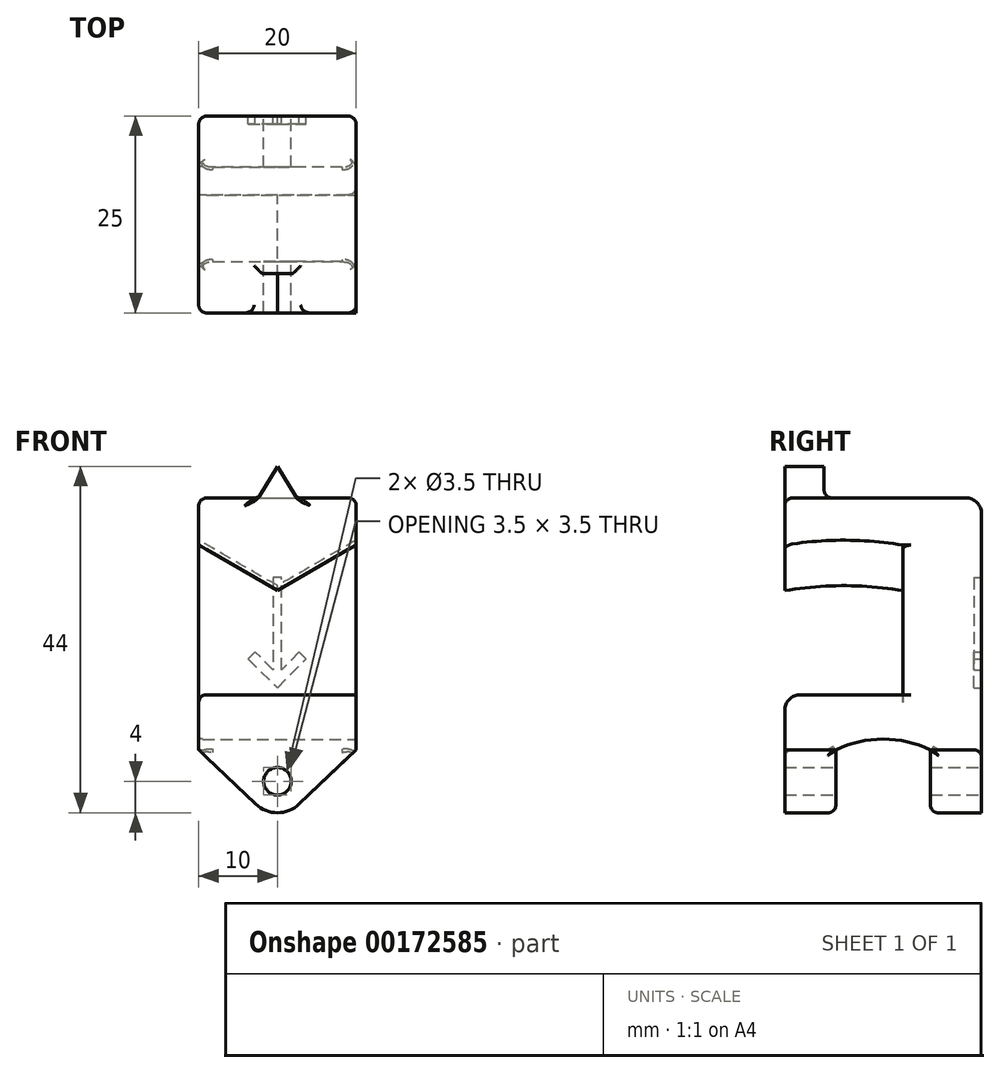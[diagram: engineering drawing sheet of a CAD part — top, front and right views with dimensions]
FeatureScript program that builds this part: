
annotation { "Feature Type Name" : "Feature", "Feature Type Description" : "" }
export const myFeature = defineFeature(function(context is Context, id is Id, definition is map)
    precondition{}
    {
        {
            var Q0;
            Q0=qCreatedBy(makeId("Front.planeOp"),FACE);
            var sketch = newSketch(context, id + "F0", { "sketchPlane" : qUnion([Q0])});
            skLineSegment(sketch, "E0.bottom", {"start": v(0, 0) * mm, "end": v(20, 0) * mm});
            skLineSegment(sketch, "E0.top", {"start": v(0, 40) * mm, "end": v(20, 40) * mm});
            skLineSegment(sketch, "E0.left", {"start": v(0, 0) * mm, "end": v(0, 40) * mm});
            skLineSegment(sketch, "E0.right", {"start": v(20, 0) * mm, "end": v(20, 40) * mm});
            skSolve(sketch);
        }
        {
            var Q0;
            Q0=qSketchRegion(id+"F0",true);
            extrude(context, id + "F1", {"entities" : qUnion([Q0]), "depth" : 10 * mm});
        }
        {
            var Q0;
            Q0=makeQuery(id+"F1.opExtrude","CAP_FACE",FACE,{"disambiguationData":[OSD([sQuery(id+"F0.wireOp",EDGE,"E0.bottom"),sQuery(id+"F0.wireOp",EDGE,"E0.top"),sQuery(id+"F0.wireOp",EDGE,"E0.left"),sQuery(id+"F0.wireOp",EDGE,"E0.right")])],"isStart":false});
            var sketch = newSketch(context, id + "F2", { "sketchPlane" : qUnion([Q0])});
            skLineSegment(sketch, "E1", {"start": v(0, 40) * mm, "end": v(20, 40) * mm});
            skLineSegment(sketch, "E2", {"start": v(20, 40) * mm, "end": v(20, 34) * mm});
            skLineSegment(sketch, "E3", {"start": v(20, 34) * mm, "end": v(10, 28.23) * mm});
            skPoint(sketch, "E3.endSnap0", {"position": v(10, 40) * mm});
            skLineSegment(sketch, "E4", {"start": v(10, 28.23) * mm, "end": v(0, 34) * mm});
            skLineSegment(sketch, "E5", {"start": v(0, 34) * mm, "end": v(0, 40) * mm});
            skLineSegment(sketch, "E6.bottom", {"start": v(0, 0) * mm, "end": v(20, 0) * mm});
            skLineSegment(sketch, "E6.top", {"start": v(0, 15) * mm, "end": v(20, 15) * mm});
            skLineSegment(sketch, "E6.left", {"start": v(0, 0) * mm, "end": v(0, 15) * mm});
            skLineSegment(sketch, "E6.right", {"start": v(20, 0) * mm, "end": v(20, 15) * mm});
            skSolve(sketch);
        }
        {
            var Q0;
            Q0=qSketchRegion(id+"F2",true);
            extrude(context, id + "F3", {"entities" : qUnion([Q0]), "operationType" : NewBodyOperationType.ADD, "depth" : 15 * mm});
        }
        {
            var Q0;
            Q0=makeQuery(id+"F3.boolean.opBoolean","MERGE",FACE,{"derivedFrom":[makeQuery(id+"F1.opExtrude","SWEPT_FACE",FACE,{"disambiguationData":[OSD([sQuery(id+"F0.wireOp",EDGE,"E0.right")])]}),makeQuery(id+"F3.opExtrude","SWEPT_FACE",FACE,{"disambiguationData":[OSD([sQuery(id+"F2.wireOp",EDGE,"E2")])]}),makeQuery(id+"F3.opExtrude","SWEPT_FACE",FACE,{"disambiguationData":[OSD([sQuery(id+"F2.wireOp",EDGE,"E6.right")])]})]});
            var sketch = newSketch(context, id + "F4", { "sketchPlane" : qUnion([Q0])});
            skLineSegment(sketch, "E7.bottom", {"start": v(-18.5, 0) * mm, "end": v(-6.5, 0) * mm});
            skLineSegment(sketch, "E7.top", {"start": v(-18.5, 8) * mm, "end": v(-6.5, 8) * mm});
            skLineSegment(sketch, "E7.left", {"start": v(-18.5, 0) * mm, "end": v(-18.5, 8) * mm});
            skLineSegment(sketch, "E7.right", {"start": v(-6.5, 0) * mm, "end": v(-6.5, 8) * mm});
            skArc(sketch, "E8", {"start": v(-6.5, 8) * mm, "mid": v(-12.5, 9.35) * mm, "end": v(-18.5, 8) * mm});
            skSolve(sketch);
        }
        {
            var Q0;
            Q0=qSketchRegion(id+"F4",true);
            extrude(context, id + "F5", {"entities" : qUnion([Q0]), "operationType" : NewBodyOperationType.REMOVE, "oppositeDirection" : true, "depth" : 25 * mm});
        }
        {
            var Q0;
            Q0=makeQuery(id+"F5.boolean.opBoolean","COPY",FACE,{"derivedFrom":makeQuery(id+"F5.opExtrude","SWEPT_FACE",FACE,{"disambiguationData":[OSD([sQuery(id+"F4.wireOp",EDGE,"E7.left")])]})});
            var sketch = newSketch(context, id + "F6", { "sketchPlane" : qUnion([Q0])});
            skCircle(sketch, "E9", {"center": v(-10, 4) * mm, "radius": 1.75 * mm});
            skPoint(sketch, "E9.centerSnap0", {"position": v(-20, 4) * mm});
            skPoint(sketch, "E9.centerSnap1", {"position": v(-10, 0) * mm});
            skSolve(sketch);
        }
        {
            var Q0;
            Q0=qSketchRegion(id+"F6",true);
            extrude(context, id + "F7", {"entities" : qUnion([Q0]), "operationType" : NewBodyOperationType.REMOVE, "oppositeDirection" : true, "depth" : 25 * mm, "hasSecondDirection" : true, "secondDirectionOppositeDirection" : false, "secondDirectionDepth" : 25 * mm});
        }
        {
            var Q0;
            Q0=makeQuery(id+"F3.opExtrude","CAP_FACE",FACE,{"disambiguationData":[OSD([sQuery(id+"F2.wireOp",EDGE,"E6.bottom"),sQuery(id+"F2.wireOp",EDGE,"E6.top"),sQuery(id+"F2.wireOp",EDGE,"E6.left"),sQuery(id+"F2.wireOp",EDGE,"E6.right")])],"isStart":false});
            var sketch = newSketch(context, id + "F8", { "sketchPlane" : qUnion([Q0])});
            skArc(sketch, "E10", {"start": v(10, 0) * mm, "mid": v(11.49, 0.29) * mm, "end": v(12.76, 1.1) * mm});
            skLineSegment(sketch, "E11", {"start": v(12.76, 1.1) * mm, "end": v(20, 8) * mm});
            skLineSegment(sketch, "E12", {"start": v(10, 4) * mm, "end": v(10, 0) * mm, "construction": true});
            skLineSegment(sketch, "E13.MirrorCS", {"start": v(7.24, 1.1) * mm, "end": v(0, 8) * mm});
            skArc(sketch, "E14.MirrorCS", {"start": v(10, 0) * mm, "mid": v(8.51, 0.29) * mm, "end": v(7.24, 1.1) * mm});
            skSolve(sketch);
        }
        {
            var Q0;
            {var subQ0=sQuery(id+"F8.wireOp",EDGE,"E10");Q0=makeQuery(id+"F8.imprint","IMPRINT",FACE,{"disambiguationData":[TD([[makeQuery(id+"F8.imprint","IMPRINT",EDGE,{"derivedFrom":subQ0}),-1.0]])]});}
            var Q1;
            {var subQ0=sQuery(id+"F8.wireOp",EDGE,"E13.MirrorCS");Q1=makeQuery(id+"F8.imprint","IMPRINT",FACE,{"disambiguationData":[TD([[makeQuery(id+"F8.imprint","IMPRINT",EDGE,{"derivedFrom":subQ0}),1.0]])]});}
            extrude(context, id + "F9", {"entities" : qUnion([Q0, Q1]), "operationType" : NewBodyOperationType.REMOVE, "oppositeDirection" : true, "depth" : 25 * mm});
        }
        {
            var Q0;
            Q0=makeQuery(id+"F1.opExtrude","CAP_EDGE",EDGE,{"disambiguationData":[OSD([sQuery(id+"F0.wireOp",EDGE,"E0.top")])],"isStart":true});
            var Q1;
            Q1=makeQuery(id+"F3.opExtrude","CAP_EDGE",EDGE,{"disambiguationData":[OSD([sQuery(id+"F2.wireOp",EDGE,"E6.top")])],"isStart":true});
            var Q2;
            Q2=makeQuery(id+"F3.opExtrude","CAP_EDGE",EDGE,{"disambiguationData":[OSD([sQuery(id+"F2.wireOp",EDGE,"E6.top")])],"isStart":false});
            fillet(context, id + "F10", {"entities" : qUnion([Q0, Q1, Q2]), "radius" : 2 * mm, "tangentPropagation" : true, "allowEdgeOverflow" : false});
        }
        {
            var Q0;
            Q0=makeQuery(id+"F1.opExtrude","CAP_EDGE",EDGE,{"disambiguationData":[OSD([sQuery(id+"F0.wireOp",EDGE,"E0.left")])],"isStart":true});
            var Q1;
            Q1=makeQuery(id+"F1.opExtrude","CAP_EDGE",EDGE,{"disambiguationData":[OSD([sQuery(id+"F0.wireOp",EDGE,"E0.right")])],"isStart":true});
            var Q2;
            Q2=makeQuery(id+"F9.boolean.opBoolean","COPY",EDGE,{"derivedFrom":makeQuery(id+"F9.opExtrude","CAP_EDGE",EDGE,{"disambiguationData":[OSD([sQuery(id+"F8.wireOp",EDGE,"E13.MirrorCS")])],"isStart":false})});
            var Q3;
            Q3=makeQuery(id+"F9.boolean.opBoolean","COPY",EDGE,{"derivedFrom":makeQuery(id+"F9.opExtrude","CAP_EDGE",EDGE,{"disambiguationData":[OSD([sQuery(id+"F8.wireOp",EDGE,"E13.MirrorCS")])],"isStart":true})});
            var Q4;
            Q4=makeQuery(id+"F9.boolean.opBoolean","INTERSECT",EDGE,{"derivedFrom":[makeQuery(id+"F5.boolean.opBoolean","COPY",FACE,{"derivedFrom":makeQuery(id+"F5.opExtrude","SWEPT_FACE",FACE,{"disambiguationData":[OSD([sQuery(id+"F4.wireOp",EDGE,"E7.right")])]})}),makeQuery(id+"F9.opExtrude","SWEPT_FACE",FACE,{"disambiguationData":[OSD([sQuery(id+"F8.wireOp",EDGE,"E13.MirrorCS")])]})]});
            var Q5;
            Q5=makeQuery(id+"F9.boolean.opBoolean","INTERSECT",EDGE,{"derivedFrom":[makeQuery(id+"F5.boolean.opBoolean","COPY",FACE,{"derivedFrom":makeQuery(id+"F5.opExtrude","SWEPT_FACE",FACE,{"disambiguationData":[OSD([sQuery(id+"F4.wireOp",EDGE,"E7.left")])]})}),makeQuery(id+"F9.opExtrude","SWEPT_FACE",FACE,{"disambiguationData":[OSD([sQuery(id+"F8.wireOp",EDGE,"E13.MirrorCS")])]})]});
            var Q6;
            Q6=makeQuery(id+"F3.opExtrude","SWEPT_EDGE",EDGE,{"disambiguationData":[OSD([sQuery(id+"F0.wireOp",EDGE,"E0.left"),sQuery(id+"F2.wireOp",EDGE,"E6.top"),sQuery(id+"F2.wireOp",EDGE,"E6.left")])]});
            var Q7;
            Q7=makeQuery(id+"F1.opExtrude","CAP_EDGE",EDGE,{"disambiguationData":[OSD([sQuery(id+"F0.wireOp",EDGE,"E0.right")])],"isStart":false});
            var Q8;
            Q8=makeQuery(id+"F3.opExtrude","CAP_EDGE",EDGE,{"disambiguationData":[OSD([sQuery(id+"F2.wireOp",EDGE,"E5")])],"isStart":false});
            var Q9;
            Q9=makeQuery(id+"F3.opExtrude","CAP_EDGE",EDGE,{"disambiguationData":[OSD([sQuery(id+"F2.wireOp",EDGE,"E1")])],"isStart":false});
            var Q10;
            Q10=makeQuery(id+"F3.opExtrude","CAP_EDGE",EDGE,{"disambiguationData":[OSD([sQuery(id+"F2.wireOp",EDGE,"E2")])],"isStart":false});
            fillet(context, id + "F11", {"entities" : qUnion([Q0, Q1, Q2, Q3, Q4, Q5, Q6, Q7, Q8, Q9, Q10]), "radius" : 1 * mm, "tangentPropagation" : true, "allowEdgeOverflow" : false});
        }
        {
            var Q0;
            Q0=makeQuery(id+"F5.boolean.opBoolean","COPY",EDGE,{"derivedFrom":makeQuery(id+"F5.opExtrude","SWEPT_EDGE",EDGE,{"disambiguationData":[OSD([sQuery(id+"F4.wireOp",EDGE,"E7.top"),sQuery(id+"F4.wireOp",EDGE,"E7.right")])]})});
            var Q1;
            Q1=makeQuery(id+"F5.boolean.opBoolean","COPY",EDGE,{"derivedFrom":makeQuery(id+"F5.opExtrude","SWEPT_EDGE",EDGE,{"disambiguationData":[OSD([sQuery(id+"F4.wireOp",EDGE,"E7.top"),sQuery(id+"F4.wireOp",EDGE,"E7.left")])]})});
            fillet(context, id + "F12", {"entities" : qUnion([Q0, Q1]), "radius" : 0.5 * mm, "tangentPropagation" : true, "allowEdgeOverflow" : false});
        }
        {
            var Q0;
            Q0=makeQuery(id+"F1.opExtrude","CAP_FACE",FACE,{"disambiguationData":[OSD([sQuery(id+"F0.wireOp",EDGE,"E0.bottom"),sQuery(id+"F0.wireOp",EDGE,"E0.top"),sQuery(id+"F0.wireOp",EDGE,"E0.left"),sQuery(id+"F0.wireOp",EDGE,"E0.right")])],"isStart":true});
            var sketch = newSketch(context, id + "F13", { "sketchPlane" : qUnion([Q0])});
            skLineSegment(sketch, "E15", {"start": v(-9.46, 29.87) * mm, "end": v(-9.46, 18.15) * mm});
            skLineSegment(sketch, "E16", {"start": v(-9.46, 18.15) * mm, "end": v(-7.17, 20.42) * mm});
            skLineSegment(sketch, "E17", {"start": v(-7.17, 20.42) * mm, "end": v(-6.3, 19.54) * mm});
            skLineSegment(sketch, "E18", {"start": v(-6.3, 19.54) * mm, "end": v(-10, 15.87) * mm});
            skLineSegment(sketch, "E19", {"start": v(-10, 15.87) * mm, "end": v(-13.65, 19.54) * mm});
            skLineSegment(sketch, "E20", {"start": v(-13.65, 19.54) * mm, "end": v(-12.76, 20.42) * mm});
            skLineSegment(sketch, "E21", {"start": v(-12.76, 20.42) * mm, "end": v(-10.51, 18.15) * mm});
            skLineSegment(sketch, "E22", {"start": v(-10.51, 18.15) * mm, "end": v(-10.51, 29.87) * mm});
            skLineSegment(sketch, "E23", {"start": v(-10.51, 29.87) * mm, "end": v(-9.46, 29.87) * mm});
            skSolve(sketch);
        }
        {
            var Q0;
            Q0=qSketchRegion(id+"F13",true);
            extrude(context, id + "F14", {"entities" : qUnion([Q0]), "operationType" : NewBodyOperationType.REMOVE, "oppositeDirection" : true, "depth" : 1 * mm});
        }
        {
            var Q0;
            Q0=makeQuery(id+"F3.opExtrude","CAP_FACE",FACE,{"disambiguationData":[OSD([sQuery(id+"F2.wireOp",EDGE,"E1"),sQuery(id+"F2.wireOp",EDGE,"E2"),sQuery(id+"F2.wireOp",EDGE,"E3"),sQuery(id+"F2.wireOp",EDGE,"E4"),sQuery(id+"F2.wireOp",EDGE,"E5")])],"isStart":false});
            var sketch = newSketch(context, id + "F15", { "sketchPlane" : qUnion([Q0])});
            skLineSegment(sketch, "E24", {"start": v(10, 39) * mm, "end": v(13, 39) * mm});
            skLineSegment(sketch, "E25", {"start": v(13, 39) * mm, "end": v(10, 44) * mm});
            skLineSegment(sketch, "E26", {"start": v(10, 44) * mm, "end": v(7, 39) * mm});
            skLineSegment(sketch, "E27", {"start": v(7, 39) * mm, "end": v(10, 39) * mm});
            skSolve(sketch);
        }
        {
            var Q0;
            Q0=qSketchRegion(id+"F15",true);
            extrude(context, id + "F16", {"entities" : qUnion([Q0]), "operationType" : NewBodyOperationType.ADD, "oppositeDirection" : true, "depth" : 5 * mm});
        }
        {
            var Q0;
            Q0=makeQuery(id+"F16.boolean.opBoolean","INTERSECT",EDGE,{"derivedFrom":[makeQuery(id+"F3.boolean.opBoolean","MERGE",FACE,{"derivedFrom":[makeQuery(id+"F1.opExtrude","SWEPT_FACE",FACE,{"disambiguationData":[OSD([sQuery(id+"F0.wireOp",EDGE,"E0.top")])]}),makeQuery(id+"F3.opExtrude","SWEPT_FACE",FACE,{"disambiguationData":[OSD([sQuery(id+"F2.wireOp",EDGE,"E1")])]})]}),makeQuery(id+"F16.opExtrude","SWEPT_FACE",FACE,{"disambiguationData":[OSD([sQuery(id+"F15.wireOp",EDGE,"E26")])]})]});
            var Q1;
            Q1=makeQuery(id+"F16.boolean.opBoolean","INTERSECT",EDGE,{"derivedFrom":[makeQuery(id+"F3.boolean.opBoolean","MERGE",FACE,{"derivedFrom":[makeQuery(id+"F1.opExtrude","SWEPT_FACE",FACE,{"disambiguationData":[OSD([sQuery(id+"F0.wireOp",EDGE,"E0.top")])]}),makeQuery(id+"F3.opExtrude","SWEPT_FACE",FACE,{"disambiguationData":[OSD([sQuery(id+"F2.wireOp",EDGE,"E1")])]})]}),makeQuery(id+"F16.opExtrude","SWEPT_FACE",FACE,{"disambiguationData":[OSD([sQuery(id+"F15.wireOp",EDGE,"E25")])]})]});
            var Q2;
            Q2=makeQuery(id+"F16.boolean.opBoolean","INTERSECT",EDGE,{"derivedFrom":[makeQuery(id+"F3.boolean.opBoolean","MERGE",FACE,{"derivedFrom":[makeQuery(id+"F1.opExtrude","SWEPT_FACE",FACE,{"disambiguationData":[OSD([sQuery(id+"F0.wireOp",EDGE,"E0.top")])]}),makeQuery(id+"F3.opExtrude","SWEPT_FACE",FACE,{"disambiguationData":[OSD([sQuery(id+"F2.wireOp",EDGE,"E1")])]})]}),makeQuery(id+"F16.opExtrude","CAP_FACE",FACE,{"disambiguationData":[OSD([sQuery(id+"F15.wireOp",EDGE,"E24"),sQuery(id+"F15.wireOp",EDGE,"E25"),sQuery(id+"F15.wireOp",EDGE,"E26"),sQuery(id+"F15.wireOp",EDGE,"E27")])],"isStart":false})]});
            fillet(context, id + "F17", {"entities" : qUnion([Q0, Q1, Q2]), "radius" : 1 * mm, "tangentPropagation" : true, "allowEdgeOverflow" : false});
        }
        {
            var Q0;
            Q0=makeQuery(id+"F5.boolean.opBoolean","COPY",EDGE,{"derivedFrom":makeQuery(id+"F5.opExtrude","CAP_EDGE",EDGE,{"disambiguationData":[OSD([sQuery(id+"F4.wireOp",EDGE,"E8")])],"isStart":true})});
            var Q1;
            Q1=makeQuery(id+"F5.boolean.opBoolean","INTERSECT",EDGE,{"derivedFrom":[makeQuery(id+"F3.boolean.opBoolean","MERGE",FACE,{"derivedFrom":[makeQuery(id+"F1.opExtrude","SWEPT_FACE",FACE,{"disambiguationData":[OSD([sQuery(id+"F0.wireOp",EDGE,"E0.left")])]}),makeQuery(id+"F3.opExtrude","SWEPT_FACE",FACE,{"disambiguationData":[OSD([sQuery(id+"F2.wireOp",EDGE,"E5")])]}),makeQuery(id+"F3.opExtrude","SWEPT_FACE",FACE,{"disambiguationData":[OSD([sQuery(id+"F2.wireOp",EDGE,"E6.left")])]})]}),makeQuery(id+"F5.opExtrude","SWEPT_FACE",FACE,{"disambiguationData":[OSD([sQuery(id+"F4.wireOp",EDGE,"E8")])]})]});
            fillet(context, id + "F18", {"entities" : qUnion([Q0, Q1]), "radius" : 0.5 * mm, "tangentPropagation" : true, "allowEdgeOverflow" : false});
        }
        {
            var Q0;
            Q0=qCreatedBy(makeId("Right.planeOp"),FACE);
            var Q1;
            Q1=makeQuery(id+"F3.opExtrude","CAP_VERTEX",VERTEX,{"disambiguationData":[OSD([sQuery(id+"F2.wireOp",EDGE,"E3"),sQuery(id+"F2.wireOp",EDGE,"E4")])],"isStart":false});
            cPlane(context, id + "F19", {"entities" : qUnion([Q0, Q1]), "cplaneType" : CPlaneType.PLANE_POINT, "offset" : 25 * mm, "width" : 150 * mm, "height" : 150 * mm});
        }
        {
            var Q0;
            Q0=qCreatedBy(id+"F19.planeOp",FACE);
            var sketch = newSketch(context, id + "F20", { "sketchPlane" : qUnion([Q0])});
            skPoint(sketch, "E28.0", {"position": v(-25, 28.23) * mm});
            skPoint(sketch, "E29.0", {"position": v(-10, 28.23) * mm});
            skArc(sketch, "E30", {"start": v(-10, 28.23) * mm, "mid": v(-17.5, 28.86) * mm, "end": v(-25, 28.23) * mm});
            skSolve(sketch);
        }
        {
            var Q0;
            Q0=makeQuery(id+"F16.boolean.opBoolean","MERGE",FACE,{"derivedFrom":[makeQuery(id+"F3.opExtrude","CAP_FACE",FACE,{"disambiguationData":[OSD([sQuery(id+"F2.wireOp",EDGE,"E1"),sQuery(id+"F2.wireOp",EDGE,"E2"),sQuery(id+"F2.wireOp",EDGE,"E3"),sQuery(id+"F2.wireOp",EDGE,"E4"),sQuery(id+"F2.wireOp",EDGE,"E5")])],"isStart":false}),makeQuery(id+"F16.opExtrude","CAP_FACE",FACE,{"disambiguationData":[OSD([sQuery(id+"F15.wireOp",EDGE,"E24"),sQuery(id+"F15.wireOp",EDGE,"E25"),sQuery(id+"F15.wireOp",EDGE,"E26"),sQuery(id+"F15.wireOp",EDGE,"E27")])],"isStart":true})]});
            var sketch = newSketch(context, id + "F21", { "sketchPlane" : qUnion([Q0])});
            skPoint(sketch, "E31.0", {"position": v(0, 34) * mm});
            skPoint(sketch, "E32.0", {"position": v(20, 34) * mm});
            skLineSegment(sketch, "E33", {"start": v(0, 34) * mm, "end": v(10, 28.23) * mm});
            skLineSegment(sketch, "E34", {"start": v(10, 28.23) * mm, "end": v(20, 34) * mm});
            skLineSegment(sketch, "E35", {"start": v(0, 26) * mm, "end": v(0, 34) * mm});
            skLineSegment(sketch, "E36", {"start": v(20, 34) * mm, "end": v(20, 26) * mm});
            skLineSegment(sketch, "E37", {"start": v(0, 26) * mm, "end": v(20, 26) * mm});
            skSolve(sketch);
        }
        {
            var Q0;
            {var subQ9=sQuery(id+"F21.wireOp",EDGE,"E35");Q0=makeQuery(id+"F21.imprint","IMPRINT",FACE,{"disambiguationData":[TD([[makeQuery(id+"F21.imprint","IMPRINT",EDGE,{"derivedFrom":subQ9}),-1.0]])]});}
            var Q1;
            Q1=sQuery(id+"F20.wireOp",EDGE,"E30");
            sweep(context, id + "F22", {"operationType" : NewBodyOperationType.REMOVE, "profiles" : qUnion([Q0]), "path" : qUnion([Q1]), "keepProfileOrientation" : true});
        }
    });
